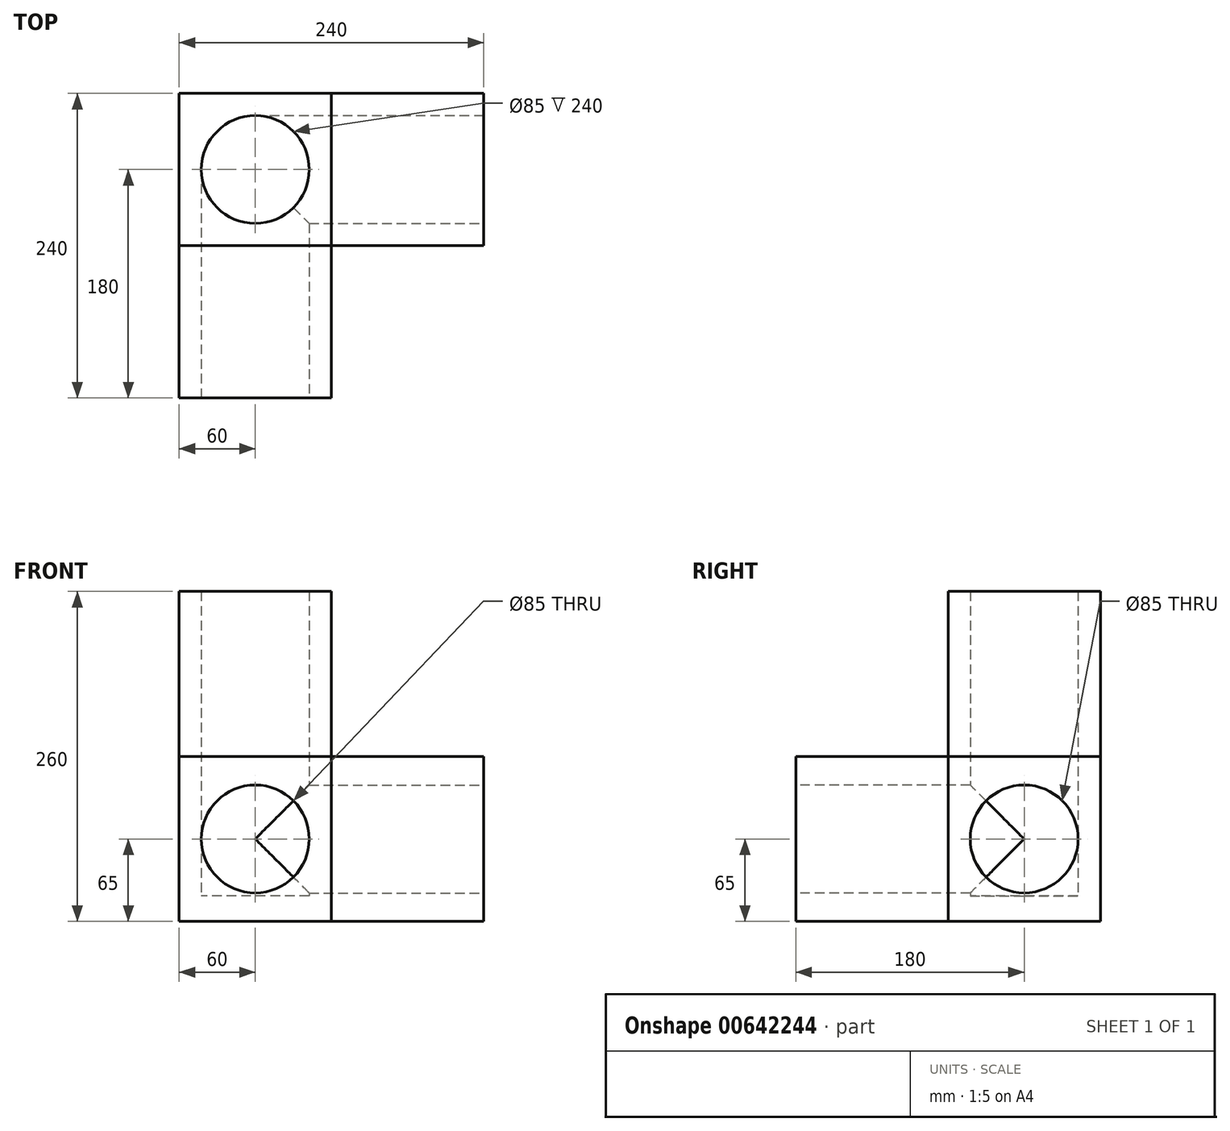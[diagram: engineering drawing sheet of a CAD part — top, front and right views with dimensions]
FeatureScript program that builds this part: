
annotation { "Feature Type Name" : "Feature", "Feature Type Description" : "" }
export const myFeature = defineFeature(function(context is Context, id is Id, definition is map)
    precondition{}
    {
        {
            var Q0;
            Q0=qCreatedBy(makeId("Top.planeOp"),FACE);
            var sketch = newSketch(context, id + "F0", { "sketchPlane" : qUnion([Q0])});
            skLineSegment(sketch, "E0.bottom", {"start": v(60, -60) * mm, "end": v(-60, -60) * mm});
            skLineSegment(sketch, "E0.top", {"start": v(60, 60) * mm, "end": v(-60, 60) * mm});
            skLineSegment(sketch, "E0.left", {"start": v(60, -60) * mm, "end": v(60, 60) * mm});
            skLineSegment(sketch, "E0.right", {"start": v(-60, -60) * mm, "end": v(-60, 60) * mm});
            skPoint(sketch, "E0.middle", {"position": v(0, 0) * mm});
            skCircle(sketch, "E1", {"center": v(0, 0) * mm, "radius": 42.5 * mm});
            skLineSegment(sketch, "E2.MirrorCS", {"start": v(60, 60) * mm, "end": v(180, 60) * mm});
            skLineSegment(sketch, "E3.MirrorCS", {"start": v(180, -60) * mm, "end": v(180, 60) * mm});
            skLineSegment(sketch, "E4.MirrorCS", {"start": v(60, -60) * mm, "end": v(180, -60) * mm});
            skLineSegment(sketch, "E5.MirrorCS", {"start": v(60, -180) * mm, "end": v(-60, -180) * mm});
            skLineSegment(sketch, "E6.MirrorCS", {"start": v(-60, -60) * mm, "end": v(-60, -180) * mm});
            skLineSegment(sketch, "E7.MirrorCS", {"start": v(60, -60) * mm, "end": v(60, -180) * mm});
            skSolve(sketch);
        }
        {
            var Q0;
            Q0=makeQuery(id+"F0.imprint","IMPRINT",FACE,{"disambiguationData":[TD([[makeQuery(id+"F0.imprint","IMPRINT",EDGE,{"derivedFrom":sQuery(id+"F0.wireOp",EDGE,"E0.bottom")}),-1.0]])]});
            extrude(context, id + "F1", {"entities" : qUnion([Q0]), "depth" : 260 * mm, "offsetDistance" : 25 * mm});
        }
        {
            var Q0;
            Q0=makeQuery(id+"F0.imprint","IMPRINT",FACE,{"disambiguationData":[TD([[makeQuery(id+"F0.imprint","IMPRINT",EDGE,{"derivedFrom":sQuery(id+"F0.wireOp",EDGE,"E0.left")}),-1.0]])]});
            var Q1;
            Q1=makeQuery(id+"F0.imprint","IMPRINT",FACE,{"disambiguationData":[TD([[makeQuery(id+"F0.imprint","IMPRINT",EDGE,{"derivedFrom":sQuery(id+"F0.wireOp",EDGE,"E0.bottom")}),1.0]])]});
            extrude(context, id + "F2", {"entities" : qUnion([Q0, Q1]), "operationType" : NewBodyOperationType.ADD, "depth" : 130 * mm, "offsetDistance" : 25 * mm});
        }
        {
            var Q0;
            Q0=makeQuery(id+"F2.opExtrude","SWEPT_FACE",FACE,{"disambiguationData":[OSD([sQuery(id+"F0.wireOp",EDGE,"E5.MirrorCS")])]});
            var sketch = newSketch(context, id + "F3", { "sketchPlane" : qUnion([Q0])});
            skCircle(sketch, "E8", {"center": v(0, 65) * mm, "radius": 42.5 * mm});
            skPoint(sketch, "E8.centerSnap0", {"position": v(-60, 65) * mm});
            skPoint(sketch, "E8.centerSnap1", {"position": v(0, 130) * mm});
            skSolve(sketch);
        }
        {
            var Q0;
            Q0=makeQuery(id+"F2.opExtrude","SWEPT_FACE",FACE,{"disambiguationData":[OSD([sQuery(id+"F0.wireOp",EDGE,"E3.MirrorCS")])]});
            var sketch = newSketch(context, id + "F4", { "sketchPlane" : qUnion([Q0])});
            skCircle(sketch, "E9", {"center": v(0, 65) * mm, "radius": 42.5 * mm});
            skPoint(sketch, "E9.centerSnap0", {"position": v(-60, 65) * mm});
            skSolve(sketch);
        }
        {
            var Q0;
            Q0=makeQuery(id+"F3.imprint","IMPRINT",FACE,{"disambiguationData":[TD([[makeQuery(id+"F3.imprint","IMPRINT",EDGE,{"derivedFrom":sQuery(id+"F3.wireOp",EDGE,"E8")}),1.0]])]});
            extrude(context, id + "F5", {"entities" : qUnion([Q0]), "operationType" : NewBodyOperationType.REMOVE, "oppositeDirection" : true, "depth" : 180 * mm, "offsetDistance" : 25 * mm});
        }
        {
            var Q0;
            Q0=makeQuery(id+"F4.imprint","IMPRINT",FACE,{"disambiguationData":[TD([[makeQuery(id+"F4.imprint","IMPRINT",EDGE,{"derivedFrom":sQuery(id+"F4.wireOp",EDGE,"E9")}),1.0]])]});
            extrude(context, id + "F6", {"entities" : qUnion([Q0]), "operationType" : NewBodyOperationType.REMOVE, "oppositeDirection" : true, "depth" : 180 * mm, "offsetDistance" : 25 * mm});
        }
        {
            var Q0;
            Q0=makeQuery(id+"F0.imprint","IMPRINT",FACE,{"disambiguationData":[TD([[makeQuery(id+"F0.imprint","IMPRINT",EDGE,{"derivedFrom":sQuery(id+"F0.wireOp",EDGE,"E1")}),1.0]])]});
            extrude(context, id + "F7", {"entities" : qUnion([Q0]), "operationType" : NewBodyOperationType.ADD, "depth" : 20 * mm, "offsetDistance" : 25 * mm});
        }
    });
